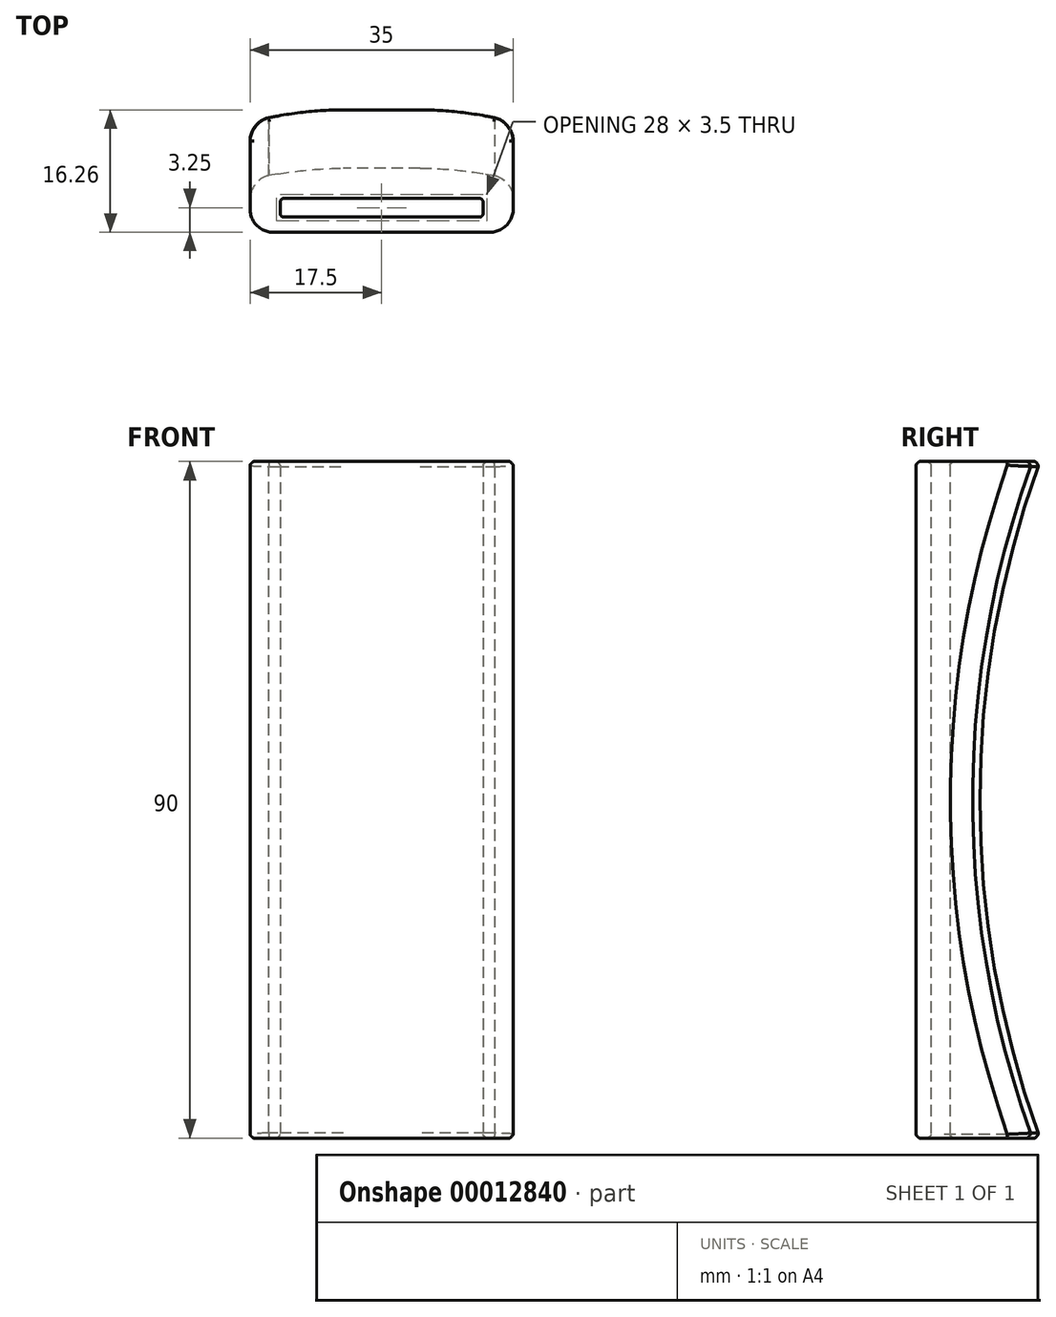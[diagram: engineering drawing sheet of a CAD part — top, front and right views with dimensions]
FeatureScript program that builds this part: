
annotation { "Feature Type Name" : "Feature", "Feature Type Description" : "" }
export const myFeature = defineFeature(function(context is Context, id is Id, definition is map)
    precondition{}
    {
        {
            var Q0;
            Q0=qCreatedBy(makeId("Top.planeOp"),FACE);
            var sketch = newSketch(context, id + "F0", { "sketchPlane" : qUnion([Q0])});
            skLineSegment(sketch, "E0.rect.bottom", {"start": v(13.5, 1.25) * mm, "end": v(-13.5, 1.25) * mm});
            skLineSegment(sketch, "E0.rect.top", {"start": v(13.5, -1.25) * mm, "end": v(-13.5, -1.25) * mm});
            skLineSegment(sketch, "E0.rect.left", {"start": v(13.5, 1.25) * mm, "end": v(13.5, -1.25) * mm});
            skLineSegment(sketch, "E0.rect.right", {"start": v(-13.5, 1.25) * mm, "end": v(-13.5, -1.25) * mm});
            skPoint(sketch, "E0.rect.middle", {"position": v(0, 0) * mm});
            skLineSegment(sketch, "E1.bottom", {"start": v(-17.5, 13.25) * mm, "end": v(17.5, 13.25) * mm});
            skLineSegment(sketch, "E1.top", {"start": v(-17.5, -3.25) * mm, "end": v(17.5, -3.25) * mm});
            skLineSegment(sketch, "E1.left", {"start": v(-17.5, 13.25) * mm, "end": v(-17.5, -3.25) * mm});
            skLineSegment(sketch, "E1.right", {"start": v(17.5, 13.25) * mm, "end": v(17.5, -3.25) * mm});
            skSolve(sketch);
        }
        {
            var Q0;
            Q0=makeQuery(id+"F0.imprint","IMPRINT",FACE,{"disambiguationData":[TD([[makeQuery(id+"F0.imprint","IMPRINT",EDGE,{"derivedFrom":sQuery(id+"F0.wireOp",EDGE,"E0.rect.bottom")}),-1.0]])]});
            extrude(context, id + "F1", {"entities" : qUnion([Q0]), "endBound" : BoundingType.SYMMETRIC, "depth" : 90 * mm});
        }
        {
            var Q0;
            Q0=qCreatedBy(makeId("Right.planeOp"),FACE);
            var sketch = newSketch(context, id + "F2", { "sketchPlane" : qUnion([Q0])});
            skLineSegment(sketch, "E2", {"start": v(13.25, -45) * mm, "end": v(13.25, 45) * mm});
            skArc(sketch, "E3", {"start": v(13.25, 45) * mm, "mid": v(5.25, 0) * mm, "end": v(13.25, -45) * mm});
            skLineSegment(sketch, "E4", {"start": v(13.25, 0) * mm, "end": v(5.25, 0) * mm});
            skSolve(sketch);
        }
        {
            var Q0;
            Q0 = qSketchRegion(id + "F2", true);
            extrude(context, id + "F3", {"entities" : qUnion([Q0]), "operationType" : NewBodyOperationType.REMOVE, "endBound" : BoundingType.THROUGH_ALL, "depth" : 25 * mm, "hasSecondDirection" : true, "secondDirectionBound" : SecondDirectionBoundingType.THROUGH_ALL, "secondDirectionOppositeDirection" : true, "secondDirectionDepth" : 25 * mm});
        }
        {
            var Q0;
            Q0=makeQuery(id+"F3.boolean.opBoolean","INTERSECT",EDGE,{"derivedFrom":[makeQuery(id+"F1.opExtrude","SWEPT_FACE",FACE,{"disambiguationData":[OSD([sQuery(id+"F0.wireOp",EDGE,"E1.right")])]}),makeQuery(id+"F3.opExtrude","SWEPT_FACE",FACE,{"disambiguationData":[OSD([sQuery(id+"F2.wireOp",EDGE,"E3")])]})]});
            var Q1;
            Q1=makeQuery(id+"F3.boolean.opBoolean","INTERSECT",EDGE,{"derivedFrom":[makeQuery(id+"F1.opExtrude","SWEPT_FACE",FACE,{"disambiguationData":[OSD([sQuery(id+"F0.wireOp",EDGE,"E1.left")])]}),makeQuery(id+"F3.opExtrude","SWEPT_FACE",FACE,{"disambiguationData":[OSD([sQuery(id+"F2.wireOp",EDGE,"E3")])]})]});
            chamfer(context, id + "F4", {"entities" : qUnion([Q0, Q1]), "chamferType" : ChamferType.OFFSET_ANGLE, "width" : 8 * mm, "oppositeDirection" : true, "angle" : 10 * degree, "tangentPropagation" : true});
        }
        {
            var Q0;
            Q0=makeQuery(id+"F1.opExtrude","SWEPT_EDGE",EDGE,{"disambiguationData":[OSD([sQuery(id+"F0.wireOp",EDGE,"E1.top"),sQuery(id+"F0.wireOp",EDGE,"E1.left")])]});
            var Q1;
            Q1=makeQuery(id+"F1.opExtrude","SWEPT_EDGE",EDGE,{"disambiguationData":[OSD([sQuery(id+"F0.wireOp",EDGE,"E1.top"),sQuery(id+"F0.wireOp",EDGE,"E1.right")])]});
            var Q2;
            {var subQ0=makeQuery(id+"F1.opExtrude","SWEPT_FACE",FACE,{"disambiguationData":[OSD([sQuery(id+"F0.wireOp",EDGE,"E1.right")])]});Q2=makeQuery(id+"F4.opChamfer","BLEND_EDGE",EDGE,{"blendedFrom":[makeQuery(id+"F3.boolean.opBoolean","INTERSECT",EDGE,{"derivedFrom":[subQ0,makeQuery(id+"F3.opExtrude","SWEPT_FACE",FACE,{"disambiguationData":[OSD([sQuery(id+"F2.wireOp",EDGE,"E3")])]})]}),subQ0],"blendedInto":[subQ0]});}
            var Q3;
            {var subQ0=makeQuery(id+"F1.opExtrude","SWEPT_FACE",FACE,{"disambiguationData":[OSD([sQuery(id+"F0.wireOp",EDGE,"E1.left")])]});Q3=makeQuery(id+"F4.opChamfer","BLEND_EDGE",EDGE,{"blendedFrom":[makeQuery(id+"F3.boolean.opBoolean","INTERSECT",EDGE,{"derivedFrom":[subQ0,makeQuery(id+"F3.opExtrude","SWEPT_FACE",FACE,{"disambiguationData":[OSD([sQuery(id+"F2.wireOp",EDGE,"E3")])]})]}),subQ0],"blendedInto":[subQ0]});}
            fillet(context, id + "F5", {"entities" : qUnion([Q0, Q1, Q2, Q3]), "radius" : 3 * mm, "tangentPropagation" : true, "rho" : .4, "crossSection" : FilletCrossSection.CONIC, "allowEdgeOverflow" : false});
        }
        {
            var Q0;
            {var subQ0=makeQuery(id+"F3.opExtrude","SWEPT_FACE",FACE,{"disambiguationData":[OSD([sQuery(id+"F2.wireOp",EDGE,"E3")])]});Q0=makeQuery(id+"F4.opChamfer","BLEND_EDGE",EDGE,{"blendedFrom":[makeQuery(id+"F3.boolean.opBoolean","INTERSECT",EDGE,{"derivedFrom":[makeQuery(id+"F1.opExtrude","SWEPT_FACE",FACE,{"disambiguationData":[OSD([sQuery(id+"F0.wireOp",EDGE,"E1.right")])]}),subQ0]}),makeQuery(id+"F3.boolean.opBoolean","COPY",FACE,{"derivedFrom":subQ0})],"blendedInto":[makeQuery(id+"F3.boolean.opBoolean","COPY",FACE,{"derivedFrom":subQ0})]});}
            var Q1;
            {var subQ0=makeQuery(id+"F3.opExtrude","SWEPT_FACE",FACE,{"disambiguationData":[OSD([sQuery(id+"F2.wireOp",EDGE,"E3")])]});Q1=makeQuery(id+"F4.opChamfer","BLEND_EDGE",EDGE,{"blendedFrom":[makeQuery(id+"F3.boolean.opBoolean","INTERSECT",EDGE,{"derivedFrom":[makeQuery(id+"F1.opExtrude","SWEPT_FACE",FACE,{"disambiguationData":[OSD([sQuery(id+"F0.wireOp",EDGE,"E1.left")])]}),subQ0]}),makeQuery(id+"F3.boolean.opBoolean","COPY",FACE,{"derivedFrom":subQ0})],"blendedInto":[makeQuery(id+"F3.boolean.opBoolean","COPY",FACE,{"derivedFrom":subQ0})]});}
            fillet(context, id + "F6", {"entities" : qUnion([Q0, Q1]), "radius" : 50 * mm, "tangentPropagation" : true, "allowEdgeOverflow" : false});
        }
        {
            var Q0;
            Q0=makeQuery(id+"F1.opExtrude","SWEPT_EDGE",EDGE,{"disambiguationData":[OSD([sQuery(id+"F0.wireOp",EDGE,"E0.rect.top"),sQuery(id+"F0.wireOp",EDGE,"E0.rect.left")])]});
            var Q1;
            Q1=makeQuery(id+"F1.opExtrude","SWEPT_EDGE",EDGE,{"disambiguationData":[OSD([sQuery(id+"F0.wireOp",EDGE,"E0.rect.bottom"),sQuery(id+"F0.wireOp",EDGE,"E0.rect.left")])]});
            var Q2;
            Q2=makeQuery(id+"F1.opExtrude","SWEPT_EDGE",EDGE,{"disambiguationData":[OSD([sQuery(id+"F0.wireOp",EDGE,"E0.rect.top"),sQuery(id+"F0.wireOp",EDGE,"E0.rect.right")])]});
            var Q3;
            Q3=makeQuery(id+"F1.opExtrude","SWEPT_EDGE",EDGE,{"disambiguationData":[OSD([sQuery(id+"F0.wireOp",EDGE,"E0.rect.bottom"),sQuery(id+"F0.wireOp",EDGE,"E0.rect.right")])]});
            fillet(context, id + "F7", {"entities" : qUnion([Q0, Q1, Q2, Q3]), "radius" : .5 * mm, "tangentPropagation" : true, "allowEdgeOverflow" : false});
        }
        {
            var Q0;
            Q0=makeQuery(id+"F1.opExtrude","CAP_FACE",FACE,{"disambiguationData":[OSD([sQuery(id+"F0.wireOp",EDGE,"E0.rect.bottom"),sQuery(id+"F0.wireOp",EDGE,"E0.rect.top"),sQuery(id+"F0.wireOp",EDGE,"E0.rect.left"),sQuery(id+"F0.wireOp",EDGE,"E0.rect.right"),sQuery(id+"F0.wireOp",EDGE,"E1.bottom"),sQuery(id+"F0.wireOp",EDGE,"E1.top"),sQuery(id+"F0.wireOp",EDGE,"E1.left"),sQuery(id+"F0.wireOp",EDGE,"E1.right")])],"isStart":true});
            var Q1;
            Q1=makeQuery(id+"F1.opExtrude","CAP_FACE",FACE,{"disambiguationData":[OSD([sQuery(id+"F0.wireOp",EDGE,"E0.rect.bottom"),sQuery(id+"F0.wireOp",EDGE,"E0.rect.top"),sQuery(id+"F0.wireOp",EDGE,"E0.rect.left"),sQuery(id+"F0.wireOp",EDGE,"E0.rect.right"),sQuery(id+"F0.wireOp",EDGE,"E1.bottom"),sQuery(id+"F0.wireOp",EDGE,"E1.top"),sQuery(id+"F0.wireOp",EDGE,"E1.left"),sQuery(id+"F0.wireOp",EDGE,"E1.right")])],"isStart":false});
            fillet(context, id + "F8", {"entities" : qUnion([Q0, Q1]), "radius" : .5 * mm, "tangentPropagation" : true, "rho" : .2, "crossSection" : FilletCrossSection.CONIC, "allowEdgeOverflow" : false});
        }
    });
